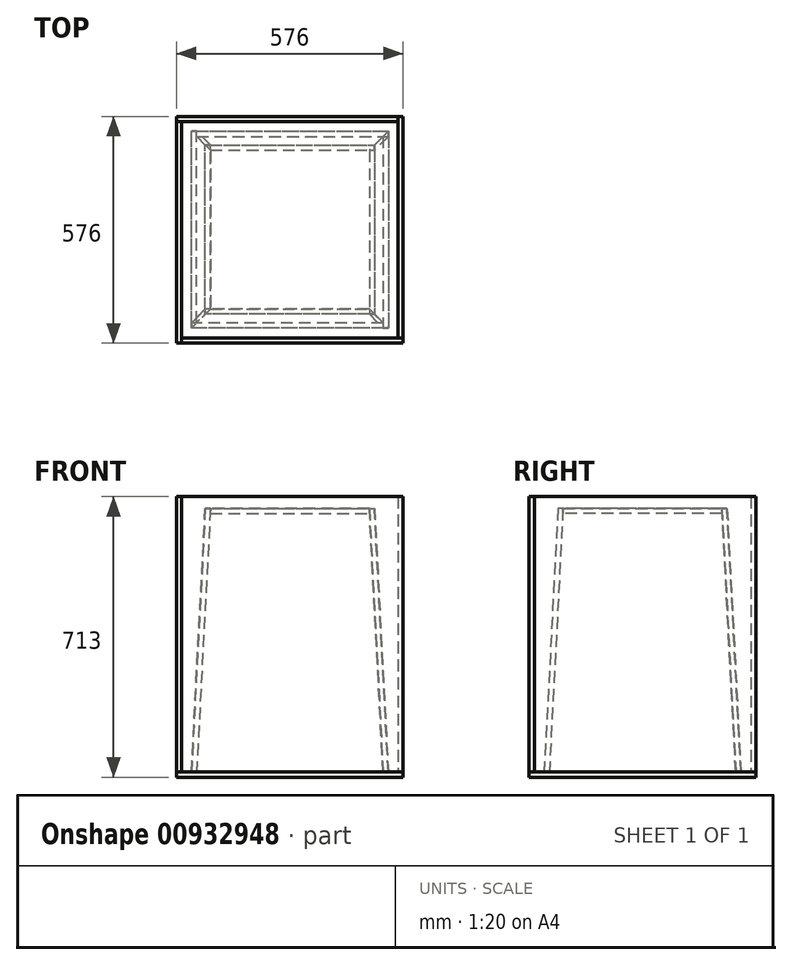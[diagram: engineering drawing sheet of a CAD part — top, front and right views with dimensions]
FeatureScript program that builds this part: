
annotation { "Feature Type Name" : "Feature", "Feature Type Description" : "" }
export const myFeature = defineFeature(function(context is Context, id is Id, definition is map)
    precondition{}
    {
        {
            var Q0;
            Q0=qCreatedBy(makeId("Top.planeOp"),FACE);
            var sketch = newSketch(context, id + "F0", { "sketchPlane" : qUnion([Q0])});
            skLineSegment(sketch, "E0.bottom", {"start": v(-275, 275) * mm, "end": v(275, 275) * mm});
            skLineSegment(sketch, "E0.top", {"start": v(-275, -275) * mm, "end": v(275, -275) * mm});
            skLineSegment(sketch, "E0.left", {"start": v(-275, 275) * mm, "end": v(-275, -275) * mm});
            skLineSegment(sketch, "E0.right", {"start": v(275, 275) * mm, "end": v(275, -275) * mm});
            skSolve(sketch);
        }
        {
            var Q0;
            Q0 = qSketchRegion(id + "F0", true);
            extrude(context, id + "F1", {"entities" : qUnion([Q0]), "depth" : 700 * mm, "offsetDistance" : 25 * mm});
        }
        {
            var Q0;
            Q0=qCreatedBy(makeId("Top.planeOp"),FACE);
            var sketch = newSketch(context, id + "F2", { "sketchPlane" : qUnion([Q0])});
            skLineSegment(sketch, "E1.bottom", {"start": v(250, 250) * mm, "end": v(-250, 250) * mm});
            skLineSegment(sketch, "E1.top", {"start": v(250, -250) * mm, "end": v(-250, -250) * mm});
            skLineSegment(sketch, "E1.left", {"start": v(250, 250) * mm, "end": v(250, -250) * mm});
            skLineSegment(sketch, "E1.right", {"start": v(-250, 250) * mm, "end": v(-250, -250) * mm});
            skSolve(sketch);
        }
        {
            var Q0;
            Q0=makeQuery(id+"F2.imprint","IMPRINT",FACE,{"disambiguationData":[TD([[makeQuery(id+"F2.imprint","IMPRINT",EDGE,{"derivedFrom":sQuery(id+"F2.wireOp",EDGE,"E1.bottom")}),1.0]])]});
            extrude(context, id + "F3", {"entities" : qUnion([Q0]), "operationType" : NewBodyOperationType.REMOVE, "depth" : 670 * mm, "offsetDistance" : 25 * mm, "hasDraft" : true, "draftAngle" : 3 * degree, "draftPullDirection" : true});
        }
        {
            var Q0;
            Q0=makeQuery(id+"F3.boolean.opBoolean","COPY",FACE,{"derivedFrom":makeQuery(id+"F3.opExtrude","SWEPT_FACE",FACE,{"disambiguationData":[OSD([sQuery(id+"F2.wireOp",EDGE,"E1.top")])]})});
            var sketch = newSketch(context, id + "F4", { "sketchPlane" : qUnion([Q0])});
            skLineSegment(sketch, "E2", {"start": v(250, -13.08) * mm, "end": v(214.89, 657.84) * mm});
            skLineSegment(sketch, "E3", {"start": v(-201.87, 657.84) * mm, "end": v(-236.98, -13.08) * mm});
            skLineSegment(sketch, "E4", {"start": v(-236.98, -13.08) * mm, "end": v(250, -13.08) * mm});
            skLineSegment(sketch, "E5", {"start": v(-201.87, 657.84) * mm, "end": v(214.89, 657.84) * mm});
            skSolve(sketch);
        }
        {
            var Q0;
            Q0 = qSketchRegion(id + "F4", true);
            extrude(context, id + "F5", {"entities" : qUnion([Q0]), "depth" : 13 * mm, "offsetDistance" : 25 * mm});
        }
        {
            var Q0;
            Q0=makeQuery(id+"F3.boolean.opBoolean","COPY",FACE,{"derivedFrom":makeQuery(id+"F3.opExtrude","SWEPT_FACE",FACE,{"disambiguationData":[OSD([sQuery(id+"F2.wireOp",EDGE,"E1.left")])]})});
            var sketch = newSketch(context, id + "F6", { "sketchPlane" : qUnion([Q0])});
            skLineSegment(sketch, "E6", {"start": v(250, -13.08) * mm, "end": v(-236.98, -13.08) * mm});
            skLineSegment(sketch, "E7", {"start": v(-236.98, -13.08) * mm, "end": v(-201.87, 657.84) * mm});
            skLineSegment(sketch, "E8", {"start": v(-201.87, 657.84) * mm, "end": v(214.89, 657.84) * mm});
            skLineSegment(sketch, "E9", {"start": v(214.89, 657.84) * mm, "end": v(250, -13.08) * mm});
            skSolve(sketch);
        }
        {
            var Q0;
            Q0 = qSketchRegion(id + "F6", true);
            extrude(context, id + "F7", {"entities" : qUnion([Q0]), "depth" : 13 * mm, "offsetDistance" : 25 * mm});
        }
        {
            var Q0;
            Q0=makeQuery(id+"F3.boolean.opBoolean","COPY",FACE,{"derivedFrom":makeQuery(id+"F3.opExtrude","SWEPT_FACE",FACE,{"disambiguationData":[OSD([sQuery(id+"F2.wireOp",EDGE,"E1.bottom")])]})});
            var sketch = newSketch(context, id + "F8", { "sketchPlane" : qUnion([Q0])});
            skLineSegment(sketch, "E10", {"start": v(250, -13.08) * mm, "end": v(214.89, 657.84) * mm});
            skLineSegment(sketch, "E11", {"start": v(214.89, 657.84) * mm, "end": v(-201.87, 657.84) * mm});
            skLineSegment(sketch, "E12", {"start": v(-201.87, 657.84) * mm, "end": v(-236.98, -13.08) * mm});
            skLineSegment(sketch, "E13", {"start": v(-236.98, -13.08) * mm, "end": v(250, -13.08) * mm});
            skSolve(sketch);
        }
        {
            var Q0;
            Q0 = qSketchRegion(id + "F8", true);
            extrude(context, id + "F9", {"entities" : qUnion([Q0]), "depth" : 13 * mm, "offsetDistance" : 25 * mm});
        }
        {
            var Q0;
            Q0=makeQuery(id+"F3.boolean.opBoolean","COPY",FACE,{"derivedFrom":makeQuery(id+"F3.opExtrude","SWEPT_FACE",FACE,{"disambiguationData":[OSD([sQuery(id+"F2.wireOp",EDGE,"E1.right")])]})});
            var sketch = newSketch(context, id + "F10", { "sketchPlane" : qUnion([Q0])});
            skLineSegment(sketch, "E14", {"start": v(250, -13.08) * mm, "end": v(214.89, 657.84) * mm});
            skLineSegment(sketch, "E15", {"start": v(214.89, 657.84) * mm, "end": v(-201.87, 657.84) * mm});
            skLineSegment(sketch, "E16", {"start": v(-201.87, 657.84) * mm, "end": v(-236.98, -13.08) * mm});
            skLineSegment(sketch, "E17", {"start": v(-236.98, -13.08) * mm, "end": v(250, -13.08) * mm});
            skSolve(sketch);
        }
        {
            var Q0;
            Q0 = qSketchRegion(id + "F10", true);
            extrude(context, id + "F11", {"entities" : qUnion([Q0]), "depth" : 13 * mm, "offsetDistance" : 25 * mm});
        }
        {
            var Q0;
            Q0=makeQuery(id+"F3.boolean.opBoolean","COPY",FACE,{"derivedFrom":makeQuery(id+"F3.opExtrude","CAP_FACE",FACE,{"disambiguationData":[OSD([sQuery(id+"F2.wireOp",EDGE,"E1.bottom"),sQuery(id+"F2.wireOp",EDGE,"E1.top"),sQuery(id+"F2.wireOp",EDGE,"E1.left"),sQuery(id+"F2.wireOp",EDGE,"E1.right")])],"isStart":false})});
            var sketch = newSketch(context, id + "F12", { "sketchPlane" : qUnion([Q0])});
            skLineSegment(sketch, "E18.bottom", {"start": v(-201.9, -201.9) * mm, "end": v(201.9, -201.9) * mm});
            skLineSegment(sketch, "E18.top", {"start": v(-201.9, 201.9) * mm, "end": v(201.9, 201.9) * mm});
            skLineSegment(sketch, "E18.left", {"start": v(-201.9, -201.9) * mm, "end": v(-201.9, 201.9) * mm});
            skLineSegment(sketch, "E18.right", {"start": v(201.9, -201.9) * mm, "end": v(201.9, 201.9) * mm});
            skSolve(sketch);
        }
        {
            var Q0;
            Q0 = qSketchRegion(id + "F12", true);
            extrude(context, id + "F13", {"entities" : qUnion([Q0]), "depth" : 13 * mm, "offsetDistance" : 25 * mm});
        }
        {
            var Q0;
            Q0=makeQuery(id+"F1.opExtrude","SWEPT_FACE",FACE,{"disambiguationData":[OSD([sQuery(id+"F0.wireOp",EDGE,"E0.bottom")])]});
            var sketch = newSketch(context, id + "F14", { "sketchPlane" : qUnion([Q0])});
            skLineSegment(sketch, "E19", {"start": v(-275, 700) * mm, "end": v(-275, 0) * mm});
            skLineSegment(sketch, "E20", {"start": v(-275, 0) * mm, "end": v(288, 0) * mm});
            skLineSegment(sketch, "E21", {"start": v(288, 0) * mm, "end": v(288, 700) * mm});
            skLineSegment(sketch, "E22", {"start": v(288, 700) * mm, "end": v(-275, 700) * mm});
            skSolve(sketch);
        }
        {
            var Q0;
            Q0 = qSketchRegion(id + "F14", true);
            extrude(context, id + "F15", {"entities" : qUnion([Q0]), "depth" : 13 * mm, "offsetDistance" : 25 * mm});
        }
        {
            var Q0;
            Q0=makeQuery(id+"F1.opExtrude","SWEPT_FACE",FACE,{"disambiguationData":[OSD([sQuery(id+"F0.wireOp",EDGE,"E0.left")])]});
            var sketch = newSketch(context, id + "F16", { "sketchPlane" : qUnion([Q0])});
            skLineSegment(sketch, "E23", {"start": v(-275, 700) * mm, "end": v(-275, 0) * mm});
            skLineSegment(sketch, "E24", {"start": v(-275, 0) * mm, "end": v(288, 0) * mm});
            skLineSegment(sketch, "E25", {"start": v(288, 0) * mm, "end": v(288, 700) * mm});
            skLineSegment(sketch, "E26", {"start": v(288, 700) * mm, "end": v(-275, 700) * mm});
            skSolve(sketch);
        }
        {
            var Q0;
            Q0 = qSketchRegion(id + "F16", true);
            extrude(context, id + "F17", {"entities" : qUnion([Q0]), "depth" : 13 * mm, "offsetDistance" : 25 * mm});
        }
        {
            var Q0;
            Q0=makeQuery(id+"F1.opExtrude","SWEPT_FACE",FACE,{"disambiguationData":[OSD([sQuery(id+"F0.wireOp",EDGE,"E0.top")])]});
            var sketch = newSketch(context, id + "F18", { "sketchPlane" : qUnion([Q0])});
            skLineSegment(sketch, "E27", {"start": v(-275, 700) * mm, "end": v(-275, 0) * mm});
            skLineSegment(sketch, "E28", {"start": v(-275, 0) * mm, "end": v(288, 0) * mm});
            skLineSegment(sketch, "E29", {"start": v(288, 0) * mm, "end": v(288, 700) * mm});
            skLineSegment(sketch, "E30", {"start": v(288, 700) * mm, "end": v(-275, 700) * mm});
            skSolve(sketch);
        }
        {
            var Q0;
            Q0 = qSketchRegion(id + "F18", true);
            extrude(context, id + "F19", {"entities" : qUnion([Q0]), "depth" : 13 * mm, "offsetDistance" : 25 * mm});
        }
        {
            var Q0;
            Q0=makeQuery(id+"F1.opExtrude","SWEPT_FACE",FACE,{"disambiguationData":[OSD([sQuery(id+"F0.wireOp",EDGE,"E0.right")])]});
            var sketch = newSketch(context, id + "F20", { "sketchPlane" : qUnion([Q0])});
            skLineSegment(sketch, "E31", {"start": v(-275, 700) * mm, "end": v(-275, 0) * mm});
            skLineSegment(sketch, "E32", {"start": v(-275, 0) * mm, "end": v(288, 0) * mm});
            skLineSegment(sketch, "E33", {"start": v(288, 0) * mm, "end": v(288, 700) * mm});
            skLineSegment(sketch, "E34", {"start": v(288, 700) * mm, "end": v(-275, 700) * mm});
            skSolve(sketch);
        }
        {
            var Q0;
            Q0 = qSketchRegion(id + "F20", true);
            extrude(context, id + "F21", {"entities" : qUnion([Q0]), "depth" : 13 * mm, "offsetDistance" : 25 * mm});
        }
        {
            var Q0;
            Q0=qCreatedBy(makeId("Top.planeOp"),FACE);
            var sketch = newSketch(context, id + "F22", { "sketchPlane" : qUnion([Q0])});
            skLineSegment(sketch, "E35.bottom", {"start": v(288, -288) * mm, "end": v(-288, -288) * mm});
            skLineSegment(sketch, "E35.top", {"start": v(288, 288) * mm, "end": v(-288, 288) * mm});
            skLineSegment(sketch, "E35.left", {"start": v(288, -288) * mm, "end": v(288, 288) * mm});
            skLineSegment(sketch, "E35.right", {"start": v(-288, -288) * mm, "end": v(-288, 288) * mm});
            skSolve(sketch);
        }
        {
            var Q0;
            Q0 = qSketchRegion(id + "F22", true);
            extrude(context, id + "F23", {"entities" : qUnion([Q0]), "oppositeDirection" : true, "depth" : 13 * mm, "offsetDistance" : 25 * mm});
        }
    });
